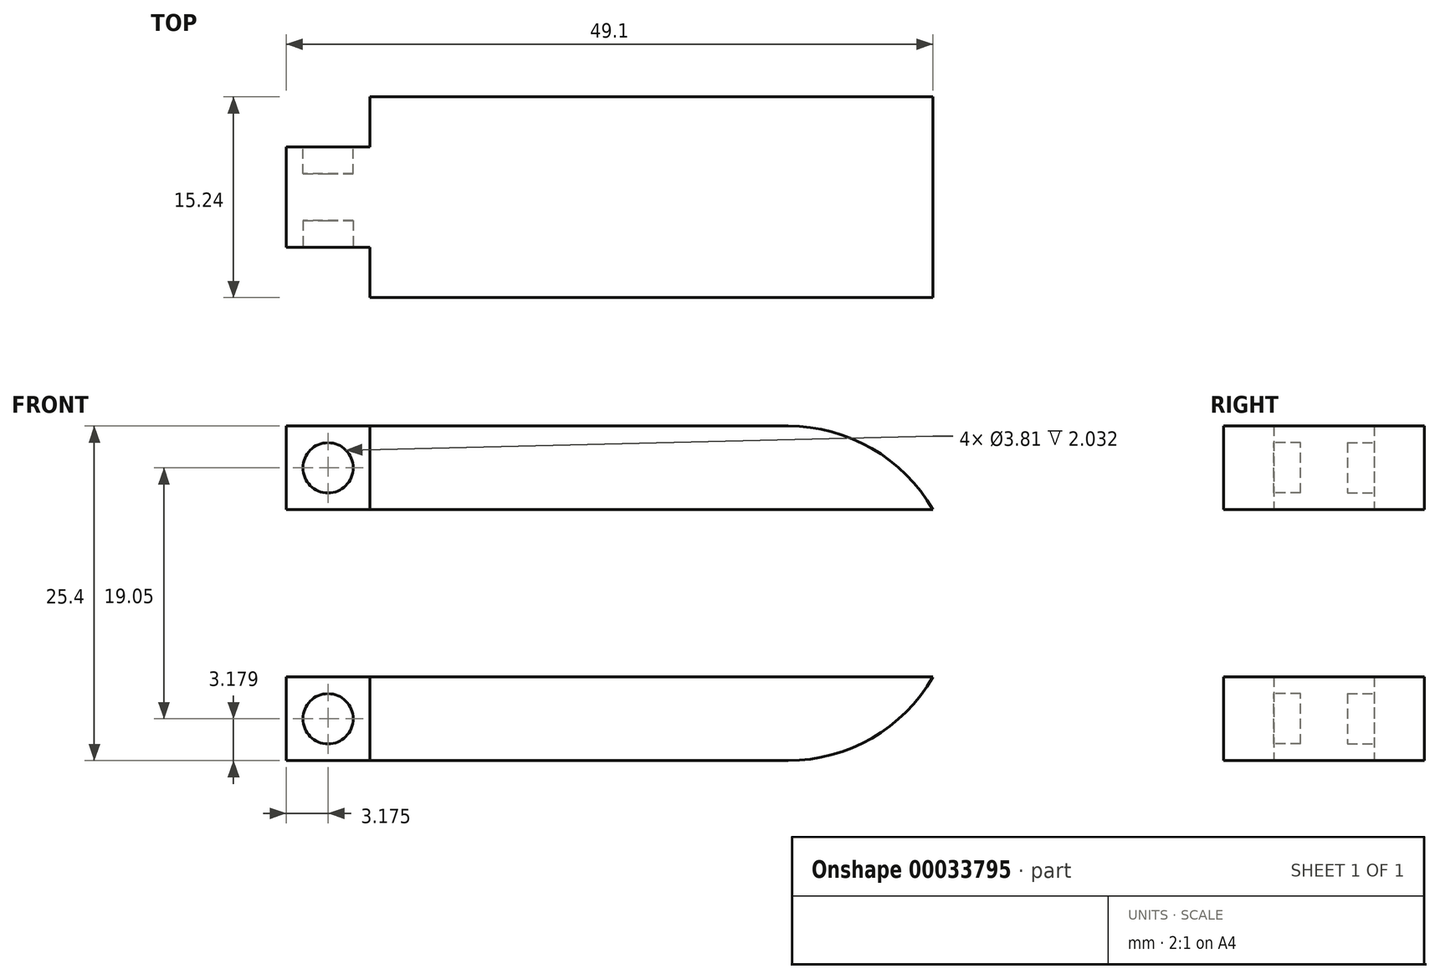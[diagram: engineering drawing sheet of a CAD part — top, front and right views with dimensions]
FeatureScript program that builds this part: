
annotation { "Feature Type Name" : "Feature", "Feature Type Description" : "" }
export const myFeature = defineFeature(function(context is Context, id is Id, definition is map)
    precondition{}
    {
        {
            var Q0;
            Q0=qCreatedBy(makeId("Right.planeOp"),FACE);
            var sketch = newSketch(context, id + "F0", { "sketchPlane" : qUnion([Q0])});
            skLineSegment(sketch, "E0.bottom", {"start": v(-16.97, 17.24) * mm, "end": v(-1.73, 17.24) * mm});
            skLineSegment(sketch, "E0.top", {"start": v(-16.97, 10.9) * mm, "end": v(-1.73, 10.9) * mm});
            skLineSegment(sketch, "E0.left", {"start": v(-16.97, 17.24) * mm, "end": v(-16.97, 10.9) * mm});
            skLineSegment(sketch, "E0.right", {"start": v(-1.73, 17.24) * mm, "end": v(-1.73, 10.9) * mm});
            skLineSegment(sketch, "E1.bottom", {"start": v(-16.97, -1.8) * mm, "end": v(-1.73, -1.8) * mm});
            skLineSegment(sketch, "E1.top", {"start": v(-16.97, -8.16) * mm, "end": v(-1.73, -8.16) * mm});
            skLineSegment(sketch, "E1.left", {"start": v(-16.97, -1.8) * mm, "end": v(-16.97, -8.16) * mm});
            skLineSegment(sketch, "E1.right", {"start": v(-1.73, -1.8) * mm, "end": v(-1.73, -8.16) * mm});
            skSolve(sketch);
        }
        {
            var Q0;
            Q0=makeQuery(id+"F0.imprint","IMPRINT",FACE,{"disambiguationData":[TD([[makeQuery(id+"F0.imprint","IMPRINT",EDGE,{"derivedFrom":sQuery(id+"F0.wireOp",EDGE,"E0.bottom")}),-1.0]])]});
            var Q1;
            Q1=makeQuery(id+"F0.imprint","IMPRINT",FACE,{"disambiguationData":[TD([[makeQuery(id+"F0.imprint","IMPRINT",EDGE,{"derivedFrom":sQuery(id+"F0.wireOp",EDGE,"E1.bottom")}),-1.0]])]});
            extrude(context, id + "F1", {"entities" : qUnion([Q0, Q1]), "oppositeDirection" : true, "depth" : 50.8 * mm});
        }
        {
            var Q0;
            Q0=makeQuery(id+"F1.opExtrude","SWEPT_FACE",FACE,{"disambiguationData":[OSD([sQuery(id+"F0.wireOp",EDGE,"E0.left")])]});
            var sketch = newSketch(context, id + "F2", { "sketchPlane" : qUnion([Q0])});
            skCircle(sketch, "E2", {"center": v(-12.7, 4.54) * mm, "radius": 12.7 * mm});
            skSolve(sketch);
        }
        {
            var Q0;
            {var subQ0=sQuery(id+"F0.wireOp",EDGE,"E0.left");var subQ4=makeQuery(id+"F1.opExtrude","CAP_EDGE",EDGE,{"disambiguationData":[OSD([subQ0])],"isStart":true});Q0=makeQuery(id+"F2.imprint","IMPRINT",FACE,{"disambiguationData":[TD([[makeQuery(id+"F2.imprint","IMPRINT",EDGE,{"derivedFrom":subQ4}),-1.0]])]});}
            extrude(context, id + "F3", {"entities" : qUnion([Q0]), "operationType" : NewBodyOperationType.REMOVE, "endBound" : BoundingType.UP_TO_NEXT, "oppositeDirection" : true, "depth" : 25.4 * mm});
        }
        {
            var Q0;
            Q0=makeQuery(id+"F1.opExtrude","SWEPT_FACE",FACE,{"disambiguationData":[OSD([sQuery(id+"F0.wireOp",EDGE,"E1.left")])]});
            var sketch = newSketch(context, id + "F4", { "sketchPlane" : qUnion([Q0])});
            skCircle(sketch, "E3", {"center": v(-12.7, 4.54) * mm, "radius": 12.7 * mm});
            skSolve(sketch);
        }
        {
            var Q0;
            {var subQ0=sQuery(id+"F0.wireOp",EDGE,"E1.left");var subQ4=makeQuery(id+"F1.opExtrude","CAP_EDGE",EDGE,{"disambiguationData":[OSD([subQ0])],"isStart":true});Q0=makeQuery(id+"F4.imprint","IMPRINT",FACE,{"disambiguationData":[TD([[makeQuery(id+"F4.imprint","IMPRINT",EDGE,{"derivedFrom":subQ4}),-1.0]])]});}
            extrude(context, id + "F5", {"entities" : qUnion([Q0]), "operationType" : NewBodyOperationType.REMOVE, "endBound" : BoundingType.UP_TO_NEXT, "oppositeDirection" : true, "depth" : 25.4 * mm});
        }
        {
            var Q0;
            Q0=makeQuery(id+"F1.opExtrude","CAP_FACE",FACE,{"disambiguationData":[OSD([sQuery(id+"F0.wireOp",EDGE,"E0.bottom"),sQuery(id+"F0.wireOp",EDGE,"E0.top"),sQuery(id+"F0.wireOp",EDGE,"E0.left"),sQuery(id+"F0.wireOp",EDGE,"E0.right")])],"isStart":false});
            var sketch = newSketch(context, id + "F6", { "sketchPlane" : qUnion([Q0])});
            skLineSegment(sketch, "E4.bottom", {"start": v(5.54, 17.24) * mm, "end": v(13.16, 17.24) * mm});
            skLineSegment(sketch, "E4.top", {"start": v(5.54, 10.9) * mm, "end": v(13.16, 10.9) * mm});
            skLineSegment(sketch, "E4.left", {"start": v(5.54, 17.24) * mm, "end": v(5.54, 10.9) * mm});
            skLineSegment(sketch, "E4.right", {"start": v(13.16, 17.24) * mm, "end": v(13.16, 10.9) * mm});
            skSolve(sketch);
        }
        {
            var Q0;
            Q0=makeQuery(id+"F1.opExtrude","CAP_FACE",FACE,{"disambiguationData":[OSD([sQuery(id+"F0.wireOp",EDGE,"E1.bottom"),sQuery(id+"F0.wireOp",EDGE,"E1.top"),sQuery(id+"F0.wireOp",EDGE,"E1.left"),sQuery(id+"F0.wireOp",EDGE,"E1.right")])],"isStart":false});
            var sketch = newSketch(context, id + "F7", { "sketchPlane" : qUnion([Q0])});
            skLineSegment(sketch, "E5.bottom", {"start": v(5.54, -1.8) * mm, "end": v(13.16, -1.8) * mm});
            skLineSegment(sketch, "E5.top", {"start": v(5.54, -8.16) * mm, "end": v(13.16, -8.16) * mm});
            skLineSegment(sketch, "E5.left", {"start": v(5.54, -1.8) * mm, "end": v(5.54, -8.16) * mm});
            skLineSegment(sketch, "E5.right", {"start": v(13.16, -1.8) * mm, "end": v(13.16, -8.16) * mm});
            skSolve(sketch);
        }
        {
            var Q0;
            {var subQ1=sQuery(id+"F6.wireOp",EDGE,"E4.left");Q0=makeQuery(id+"F6.imprint","IMPRINT",FACE,{"disambiguationData":[TD([[makeQuery(id+"F6.imprint","IMPRINT",EDGE,{"derivedFrom":subQ1}),-1.0]])]});}
            var Q1;
            {var subQ1=sQuery(id+"F6.wireOp",EDGE,"E4.right");Q1=makeQuery(id+"F6.imprint","IMPRINT",FACE,{"disambiguationData":[TD([[makeQuery(id+"F6.imprint","IMPRINT",EDGE,{"derivedFrom":subQ1}),1.0]])]});}
            extrude(context, id + "F8", {"entities" : qUnion([Q0, Q1]), "operationType" : NewBodyOperationType.REMOVE, "oppositeDirection" : true, "depth" : 6.35 * mm});
        }
        {
            var Q0;
            {var subQ1=sQuery(id+"F7.wireOp",EDGE,"E5.left");Q0=makeQuery(id+"F7.imprint","IMPRINT",FACE,{"disambiguationData":[TD([[makeQuery(id+"F7.imprint","IMPRINT",EDGE,{"derivedFrom":subQ1}),-1.0]])]});}
            var Q1;
            {var subQ1=sQuery(id+"F7.wireOp",EDGE,"E5.right");Q1=makeQuery(id+"F7.imprint","IMPRINT",FACE,{"disambiguationData":[TD([[makeQuery(id+"F7.imprint","IMPRINT",EDGE,{"derivedFrom":subQ1}),1.0]])]});}
            extrude(context, id + "F9", {"entities" : qUnion([Q0, Q1]), "operationType" : NewBodyOperationType.REMOVE, "oppositeDirection" : true, "depth" : 6.35 * mm});
        }
        {
            var Q0;
            Q0=makeQuery(id+"F8.boolean.opBoolean","COPY",FACE,{"derivedFrom":makeQuery(id+"F8.opExtrude","SWEPT_FACE",FACE,{"disambiguationData":[OSD([sQuery(id+"F6.wireOp",EDGE,"E4.right")])]})});
            var sketch = newSketch(context, id + "F10", { "sketchPlane" : qUnion([Q0])});
            skLineSegment(sketch, "E6", {"start": v(-50.8, 14.07) * mm, "end": v(-44.45, 14.07) * mm});
            skLineSegment(sketch, "E7", {"start": v(-47.62, 17.24) * mm, "end": v(-47.62, 10.9) * mm});
            skLineSegment(sketch, "E8", {"start": v(-47.62, 10.9) * mm, "end": v(-47.38, 10.78) * mm});
            skCircle(sketch, "E9", {"center": v(-47.62, 14.07) * mm, "radius": 1.9 * mm});
            skSolve(sketch);
        }
        {
            var Q0;
            Q0=makeQuery(id+"F9.boolean.opBoolean","COPY",FACE,{"derivedFrom":makeQuery(id+"F9.opExtrude","SWEPT_FACE",FACE,{"disambiguationData":[OSD([sQuery(id+"F7.wireOp",EDGE,"E5.right")])]})});
            var sketch = newSketch(context, id + "F11", { "sketchPlane" : qUnion([Q0])});
            skLineSegment(sketch, "E10", {"start": v(-50.8, -4.98) * mm, "end": v(-44.45, -4.98) * mm});
            skLineSegment(sketch, "E11", {"start": v(-47.62, -1.8) * mm, "end": v(-47.62, -8.16) * mm});
            skLineSegment(sketch, "E12", {"start": v(-47.62, -8.16) * mm, "end": v(-47.37, -8.03) * mm});
            skCircle(sketch, "E13", {"center": v(-47.62, -4.98) * mm, "radius": 1.9 * mm});
            skSolve(sketch);
        }
        {
            var Q0;
            {var subQ0=sQuery(id+"F10.wireOp",EDGE,"E9");var subQ3=sQuery(id+"F10.wireOp",EDGE,"E6");var subQ4=makeQuery(id+"F10.imprint","INTERSECT",VERTEX,{"disambiguationData":[OD(0.0)],"derivedFrom":[subQ3,subQ0]});Q0=makeQuery(id+"F10.imprint","IMPRINT",FACE,{"disambiguationData":[TD([[makeQuery(id+"F10.imprint","IMPRINT",EDGE,{"disambiguationData":[TD([[subQ4,-1.0]])],"derivedFrom":subQ3}),1.0]])]});}
            var Q1;
            {var subQ1=sQuery(id+"F10.wireOp",EDGE,"E7");var subQ3=sQuery(id+"F10.wireOp",EDGE,"E6");var subQ5=makeQuery(id+"F10.imprint","INTERSECT",VERTEX,{"derivedFrom":[subQ3,subQ1]});Q1=makeQuery(id+"F10.imprint","IMPRINT",FACE,{"disambiguationData":[TD([[makeQuery(id+"F10.imprint","IMPRINT",EDGE,{"disambiguationData":[TD([[subQ5,-1.0]])],"derivedFrom":subQ3}),1.0]])]});}
            var Q2;
            {var subQ1=sQuery(id+"F10.wireOp",EDGE,"E7");var subQ3=sQuery(id+"F10.wireOp",EDGE,"E6");var subQ5=makeQuery(id+"F10.imprint","INTERSECT",VERTEX,{"derivedFrom":[subQ3,subQ1]});Q2=makeQuery(id+"F10.imprint","IMPRINT",FACE,{"disambiguationData":[TD([[makeQuery(id+"F10.imprint","IMPRINT",EDGE,{"disambiguationData":[TD([[subQ5,-1.0]])],"derivedFrom":subQ3}),-1.0]])]});}
            var Q3;
            {var subQ0=sQuery(id+"F10.wireOp",EDGE,"E9");var subQ3=sQuery(id+"F10.wireOp",EDGE,"E6");var subQ4=makeQuery(id+"F10.imprint","INTERSECT",VERTEX,{"disambiguationData":[OD(0.0)],"derivedFrom":[subQ3,subQ0]});Q3=makeQuery(id+"F10.imprint","IMPRINT",FACE,{"disambiguationData":[TD([[makeQuery(id+"F10.imprint","IMPRINT",EDGE,{"disambiguationData":[TD([[subQ4,-1.0]])],"derivedFrom":subQ3}),-1.0]])]});}
            extrude(context, id + "F12", {"entities" : qUnion([Q0, Q1, Q2, Q3]), "operationType" : NewBodyOperationType.REMOVE, "oppositeDirection" : true, "depth" : 2.03 * mm});
        }
        {
            var Q0;
            {var subQ0=sQuery(id+"F11.wireOp",EDGE,"E13");var subQ3=sQuery(id+"F11.wireOp",EDGE,"E10");var subQ4=makeQuery(id+"F11.imprint","INTERSECT",VERTEX,{"disambiguationData":[OD(0.0)],"derivedFrom":[subQ3,subQ0]});Q0=makeQuery(id+"F11.imprint","IMPRINT",FACE,{"disambiguationData":[TD([[makeQuery(id+"F11.imprint","IMPRINT",EDGE,{"disambiguationData":[TD([[subQ4,-1.0]])],"derivedFrom":subQ3}),1.0]])]});}
            var Q1;
            {var subQ1=sQuery(id+"F11.wireOp",EDGE,"E11");var subQ3=sQuery(id+"F11.wireOp",EDGE,"E10");var subQ5=makeQuery(id+"F11.imprint","INTERSECT",VERTEX,{"derivedFrom":[subQ3,subQ1]});Q1=makeQuery(id+"F11.imprint","IMPRINT",FACE,{"disambiguationData":[TD([[makeQuery(id+"F11.imprint","IMPRINT",EDGE,{"disambiguationData":[TD([[subQ5,-1.0]])],"derivedFrom":subQ3}),1.0]])]});}
            var Q2;
            {var subQ1=sQuery(id+"F11.wireOp",EDGE,"E11");var subQ3=sQuery(id+"F11.wireOp",EDGE,"E10");var subQ5=makeQuery(id+"F11.imprint","INTERSECT",VERTEX,{"derivedFrom":[subQ3,subQ1]});Q2=makeQuery(id+"F11.imprint","IMPRINT",FACE,{"disambiguationData":[TD([[makeQuery(id+"F11.imprint","IMPRINT",EDGE,{"disambiguationData":[TD([[subQ5,-1.0]])],"derivedFrom":subQ3}),-1.0]])]});}
            var Q3;
            {var subQ0=sQuery(id+"F11.wireOp",EDGE,"E13");var subQ3=sQuery(id+"F11.wireOp",EDGE,"E10");var subQ4=makeQuery(id+"F11.imprint","INTERSECT",VERTEX,{"disambiguationData":[OD(0.0)],"derivedFrom":[subQ3,subQ0]});Q3=makeQuery(id+"F11.imprint","IMPRINT",FACE,{"disambiguationData":[TD([[makeQuery(id+"F11.imprint","IMPRINT",EDGE,{"disambiguationData":[TD([[subQ4,-1.0]])],"derivedFrom":subQ3}),-1.0]])]});}
            extrude(context, id + "F13", {"entities" : qUnion([Q0, Q1, Q2, Q3]), "operationType" : NewBodyOperationType.REMOVE, "oppositeDirection" : true, "depth" : 2.03 * mm});
        }
        {
            var Q0;
            Q0=makeQuery(id+"F8.boolean.opBoolean","COPY",FACE,{"derivedFrom":makeQuery(id+"F8.opExtrude","SWEPT_FACE",FACE,{"disambiguationData":[OSD([sQuery(id+"F6.wireOp",EDGE,"E4.left")])]})});
            var sketch = newSketch(context, id + "F14", { "sketchPlane" : qUnion([Q0])});
            skLineSegment(sketch, "E14", {"start": v(50.8, 14.07) * mm, "end": v(44.45, 14.07) * mm});
            skLineSegment(sketch, "E15", {"start": v(47.62, 17.24) * mm, "end": v(47.62, 10.9) * mm});
            skCircle(sketch, "E16", {"center": v(47.62, 14.07) * mm, "radius": 1.9 * mm});
            skSolve(sketch);
        }
        {
            var Q0;
            Q0=makeQuery(id+"F9.boolean.opBoolean","COPY",FACE,{"derivedFrom":makeQuery(id+"F9.opExtrude","SWEPT_FACE",FACE,{"disambiguationData":[OSD([sQuery(id+"F7.wireOp",EDGE,"E5.left")])]})});
            var sketch = newSketch(context, id + "F15", { "sketchPlane" : qUnion([Q0])});
            skLineSegment(sketch, "E17", {"start": v(50.8, -4.98) * mm, "end": v(44.45, -4.98) * mm});
            skLineSegment(sketch, "E18", {"start": v(47.62, -1.8) * mm, "end": v(47.62, -8.16) * mm});
            skCircle(sketch, "E19", {"center": v(47.62, -4.98) * mm, "radius": 1.9 * mm});
            skSolve(sketch);
        }
        {
            var Q0;
            {var subQ1=sQuery(id+"F14.wireOp",EDGE,"E15");var subQ3=sQuery(id+"F14.wireOp",EDGE,"E14");var subQ5=makeQuery(id+"F14.imprint","INTERSECT",VERTEX,{"derivedFrom":[subQ3,subQ1]});Q0=makeQuery(id+"F14.imprint","IMPRINT",FACE,{"disambiguationData":[TD([[makeQuery(id+"F14.imprint","IMPRINT",EDGE,{"disambiguationData":[TD([[subQ5,-1.0]])],"derivedFrom":subQ3}),-1.0]])]});}
            var Q1;
            {var subQ0=sQuery(id+"F14.wireOp",EDGE,"E16");var subQ3=sQuery(id+"F14.wireOp",EDGE,"E14");var subQ4=makeQuery(id+"F14.imprint","INTERSECT",VERTEX,{"disambiguationData":[OD(0.0)],"derivedFrom":[subQ3,subQ0]});Q1=makeQuery(id+"F14.imprint","IMPRINT",FACE,{"disambiguationData":[TD([[makeQuery(id+"F14.imprint","IMPRINT",EDGE,{"disambiguationData":[TD([[subQ4,-1.0]])],"derivedFrom":subQ3}),-1.0]])]});}
            var Q2;
            {var subQ0=sQuery(id+"F14.wireOp",EDGE,"E16");var subQ3=sQuery(id+"F14.wireOp",EDGE,"E14");var subQ4=makeQuery(id+"F14.imprint","INTERSECT",VERTEX,{"disambiguationData":[OD(0.0)],"derivedFrom":[subQ3,subQ0]});Q2=makeQuery(id+"F14.imprint","IMPRINT",FACE,{"disambiguationData":[TD([[makeQuery(id+"F14.imprint","IMPRINT",EDGE,{"disambiguationData":[TD([[subQ4,-1.0]])],"derivedFrom":subQ3}),1.0]])]});}
            var Q3;
            {var subQ1=sQuery(id+"F14.wireOp",EDGE,"E15");var subQ3=sQuery(id+"F14.wireOp",EDGE,"E14");var subQ5=makeQuery(id+"F14.imprint","INTERSECT",VERTEX,{"derivedFrom":[subQ3,subQ1]});Q3=makeQuery(id+"F14.imprint","IMPRINT",FACE,{"disambiguationData":[TD([[makeQuery(id+"F14.imprint","IMPRINT",EDGE,{"disambiguationData":[TD([[subQ5,-1.0]])],"derivedFrom":subQ3}),1.0]])]});}
            extrude(context, id + "F16", {"entities" : qUnion([Q0, Q1, Q2, Q3]), "operationType" : NewBodyOperationType.REMOVE, "oppositeDirection" : true, "depth" : 2.03 * mm});
        }
        {
            var Q0;
            {var subQ1=sQuery(id+"F15.wireOp",EDGE,"E18");var subQ3=sQuery(id+"F15.wireOp",EDGE,"E17");var subQ5=makeQuery(id+"F15.imprint","INTERSECT",VERTEX,{"derivedFrom":[subQ3,subQ1]});Q0=makeQuery(id+"F15.imprint","IMPRINT",FACE,{"disambiguationData":[TD([[makeQuery(id+"F15.imprint","IMPRINT",EDGE,{"disambiguationData":[TD([[subQ5,-1.0]])],"derivedFrom":subQ3}),-1.0]])]});}
            var Q1;
            {var subQ0=sQuery(id+"F15.wireOp",EDGE,"E19");var subQ3=sQuery(id+"F15.wireOp",EDGE,"E17");var subQ4=makeQuery(id+"F15.imprint","INTERSECT",VERTEX,{"disambiguationData":[OD(0.0)],"derivedFrom":[subQ3,subQ0]});Q1=makeQuery(id+"F15.imprint","IMPRINT",FACE,{"disambiguationData":[TD([[makeQuery(id+"F15.imprint","IMPRINT",EDGE,{"disambiguationData":[TD([[subQ4,-1.0]])],"derivedFrom":subQ3}),-1.0]])]});}
            var Q2;
            {var subQ0=sQuery(id+"F15.wireOp",EDGE,"E19");var subQ3=sQuery(id+"F15.wireOp",EDGE,"E17");var subQ4=makeQuery(id+"F15.imprint","INTERSECT",VERTEX,{"disambiguationData":[OD(0.0)],"derivedFrom":[subQ3,subQ0]});Q2=makeQuery(id+"F15.imprint","IMPRINT",FACE,{"disambiguationData":[TD([[makeQuery(id+"F15.imprint","IMPRINT",EDGE,{"disambiguationData":[TD([[subQ4,-1.0]])],"derivedFrom":subQ3}),1.0]])]});}
            var Q3;
            {var subQ1=sQuery(id+"F15.wireOp",EDGE,"E18");var subQ3=sQuery(id+"F15.wireOp",EDGE,"E17");var subQ5=makeQuery(id+"F15.imprint","INTERSECT",VERTEX,{"derivedFrom":[subQ3,subQ1]});Q3=makeQuery(id+"F15.imprint","IMPRINT",FACE,{"disambiguationData":[TD([[makeQuery(id+"F15.imprint","IMPRINT",EDGE,{"disambiguationData":[TD([[subQ5,-1.0]])],"derivedFrom":subQ3}),1.0]])]});}
            extrude(context, id + "F17", {"entities" : qUnion([Q0, Q1, Q2, Q3]), "operationType" : NewBodyOperationType.REMOVE, "oppositeDirection" : true, "depth" : 2.03 * mm});
        }
    });
